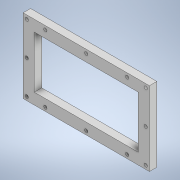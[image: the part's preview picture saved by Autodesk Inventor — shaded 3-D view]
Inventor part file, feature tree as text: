
AUTODESK INVENTOR PART (.ipt)
format: ipt  version: 2022.2 (Build 262287030, 287C)  size: 142,848 bytes
history: native  units: in
note: dims shown in document units (in); Inventor stores cm internally (conversion verified against a paired STEP export)
features: sketch x3, extrude x2, hole x1
ambient origin geometry x8: Origin, YZ Plane, XZ Plane, XY Plane, X Axis, Y Axis, Z Axis, Center Point
bodies: Solid1 (feature_tree)
feature tree (6):
  extrude  "Extrusion1"  Depth=3.937in
  extrude  "Extrusion2"  Depth=5.5118in
  hole  "Hole2"  [1 undecoded]
  sketch  "Sketch1"  dims[d0=6.6929in d1=3.937in]
  sketch  "Sketch2"  dims[d2=0.3937in d3=0.0in d4=5.5118in]
  sketch  "Sketch4"  dims[d5=2.7559in d6=0.3937in d7=0.0in d72=1.9685in d73=0.1969in d74=0.1969in d75=3.3465in d78=0.9843in d80=0.1969in d81=0.1969in d82=0.9843in d83=0.7874in d85=6.2992in d86=0.3937in d88=0.3937in d106=0.172in d107=0.2953in d108=0.1476in d109=0.0984in d110=90.0deg d111=0.1181in d112=0.0in d115=0.1969in d116=0.1969in d117=0.1969in d118=0.7874in d120=3.5433in d121=0.3937in d123=0.3937in d125=1.7717in d156=0.3937in d157=0.3937in d158=0.3937in d159=0.0591in d160=0.2283in d161=0.1476in d162=0.5635in d163=0.2953in d164=0.8108in d165=0.0246in d166=0.2953in d167=0.1476in d168=0.0591in d169=0.0984in d170=0.1476in d171=0.5635in d172=0.2953in d173=0.8108in d174=0.0246in d175=0.2953in d176=0.1476in]
note: 1 required parameter value undecoded (feature->parameter linkage not recoverable at this tier; creation-order binding heuristic only, values carry confidence <= 0.55)
